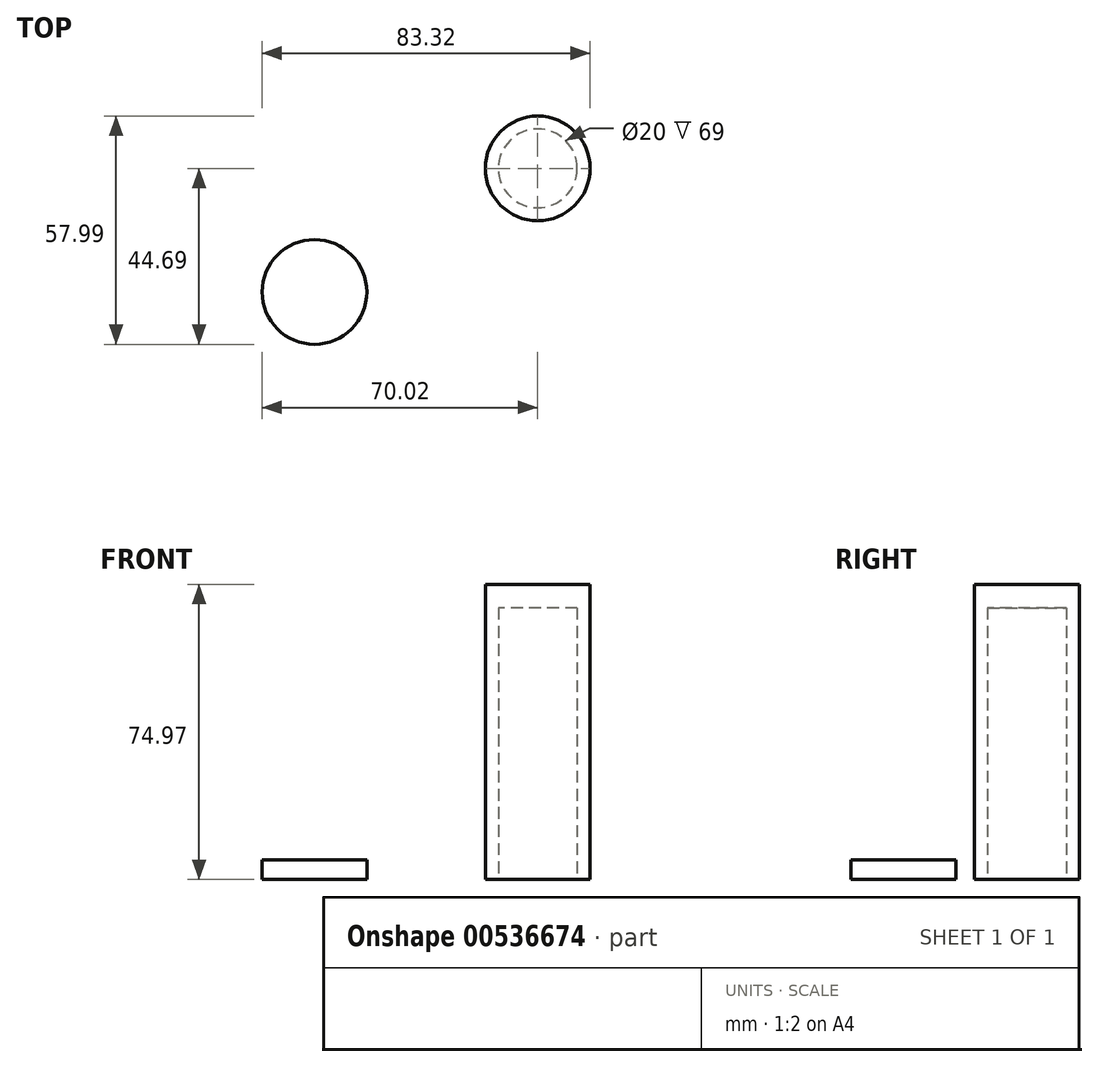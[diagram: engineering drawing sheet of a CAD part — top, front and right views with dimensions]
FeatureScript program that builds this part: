
annotation { "Feature Type Name" : "Feature", "Feature Type Description" : "" }
export const myFeature = defineFeature(function(context is Context, id is Id, definition is map)
    precondition{}
    {
        {
            var Q0;
            Q0=qCreatedBy(makeId("Top.planeOp"),FACE);
            var sketch = newSketch(context, id + "F0", { "sketchPlane" : qUnion([Q0])});
            skCircle(sketch, "E0", {"center": v(0, 0) * mm, "radius": 13.3 * mm});
            skSolve(sketch);
        }
        {
            var Q0;
            Q0=makeQuery(id+"F0.imprint","IMPRINT",FACE,{"disambiguationData":[TD([[makeQuery(id+"F0.imprint","IMPRINT",EDGE,{"derivedFrom":sQuery(id+"F0.wireOp",EDGE,"E0")}),1.0]])]});
            extrude(context, id + "F1", {"entities" : qUnion([Q0]), "depth" : 74.97 * mm, "offsetDistance" : 25 * mm});
        }
        {
            var Q0;
            Q0=qCreatedBy(makeId("Top.planeOp"),FACE);
            var sketch = newSketch(context, id + "F2", { "sketchPlane" : qUnion([Q0])});
            skCircle(sketch, "E1", {"center": v(0, 0) * mm, "radius": 10 * mm});
            skSolve(sketch);
        }
        {
            var Q0;
            Q0=makeQuery(id+"F2.imprint","IMPRINT",FACE,{"disambiguationData":[TD([[makeQuery(id+"F2.imprint","IMPRINT",EDGE,{"derivedFrom":sQuery(id+"F2.wireOp",EDGE,"E1")}),1.0]])]});
            extrude(context, id + "F3", {"entities" : qUnion([Q0]), "operationType" : NewBodyOperationType.REMOVE, "depth" : 69 * mm, "offsetDistance" : 25 * mm});
        }
        {
            var Q0;
            Q0=qCreatedBy(makeId("Top.planeOp"),FACE);
            var sketch = newSketch(context, id + "F4", { "sketchPlane" : qUnion([Q0])});
            skCircle(sketch, "E2", {"center": v(-56.72, -31.39) * mm, "radius": 13.3 * mm});
            skSolve(sketch);
        }
        {
            var Q0;
            Q0=makeQuery(id+"F4.imprint","IMPRINT",FACE,{"disambiguationData":[TD([[makeQuery(id+"F4.imprint","IMPRINT",EDGE,{"derivedFrom":sQuery(id+"F4.wireOp",EDGE,"E2")}),1.0]])]});
            extrude(context, id + "F5", {"entities" : qUnion([Q0]), "depth" : 5 * mm, "offsetDistance" : 25 * mm});
        }
    });
